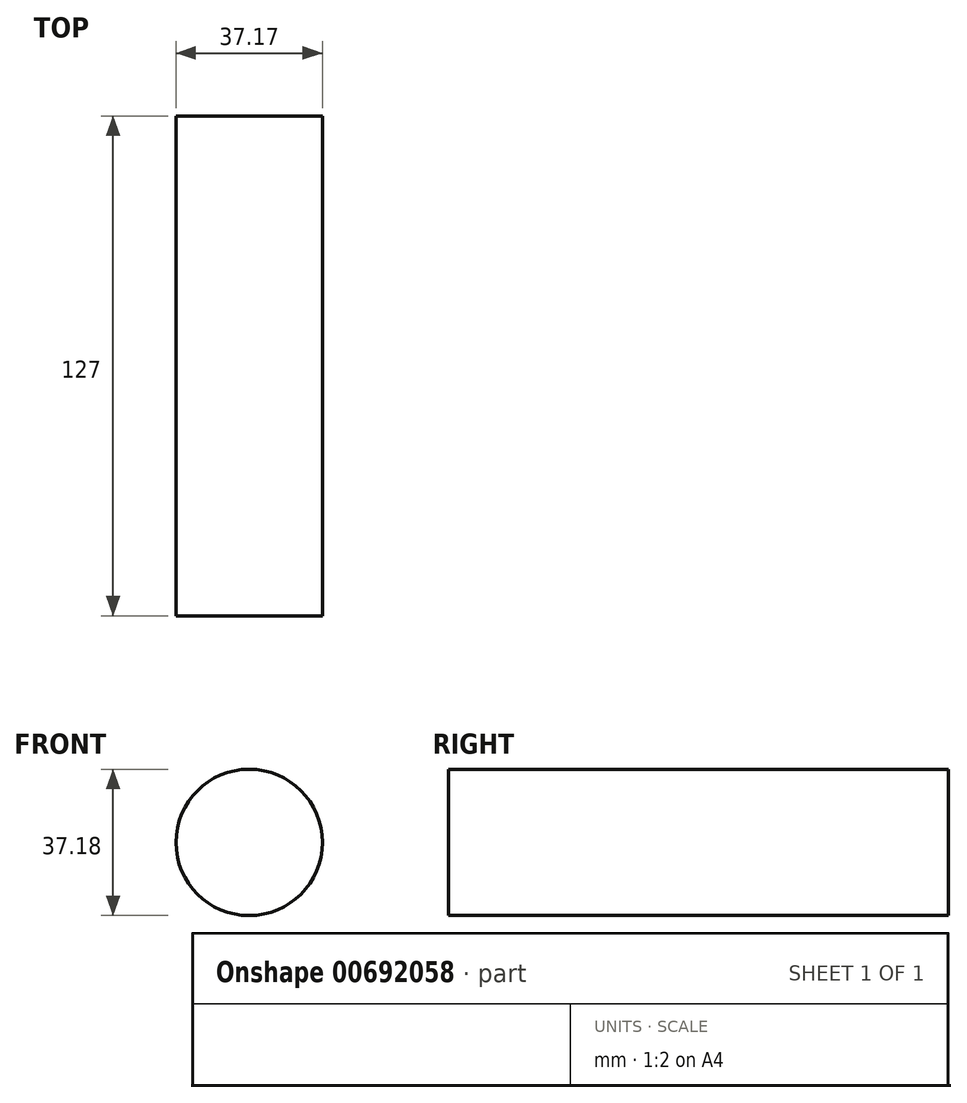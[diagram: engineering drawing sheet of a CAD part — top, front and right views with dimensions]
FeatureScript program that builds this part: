
annotation { "Feature Type Name" : "Feature", "Feature Type Description" : "" }
export const myFeature = defineFeature(function(context is Context, id is Id, definition is map)
    precondition{}
    {
        {
            var Q0;
            Q0=qCreatedBy(makeId("Front.planeOp"),FACE);
            var sketch = newSketch(context, id + "F0", { "sketchPlane" : qUnion([Q0])});
            skCircle(sketch, "E0", {"center": v(-23.9, 0) * mm, "radius": 18.59 * mm});
            skSolve(sketch);
        }
        {
            var Q0;
            Q0=makeQuery(id+"F0.imprint","IMPRINT",FACE,{"disambiguationData":[TD([[makeQuery(id+"F0.imprint","IMPRINT",EDGE,{"derivedFrom":sQuery(id+"F0.wireOp",EDGE,"E0")}),1.0]])]});
            var Q1;
            Q1=sQuery(id+"F0.wireOp",EDGE,"E0");
            extrude(context, id + "F1", {"entities" : qUnion([Q0]), "surfaceEntities" : qUnion([Q1]), "endBound" : BoundingType.SYMMETRIC, "depth" : 127 * mm, "offsetDistance" : 25.4 * mm});
        }
    });
